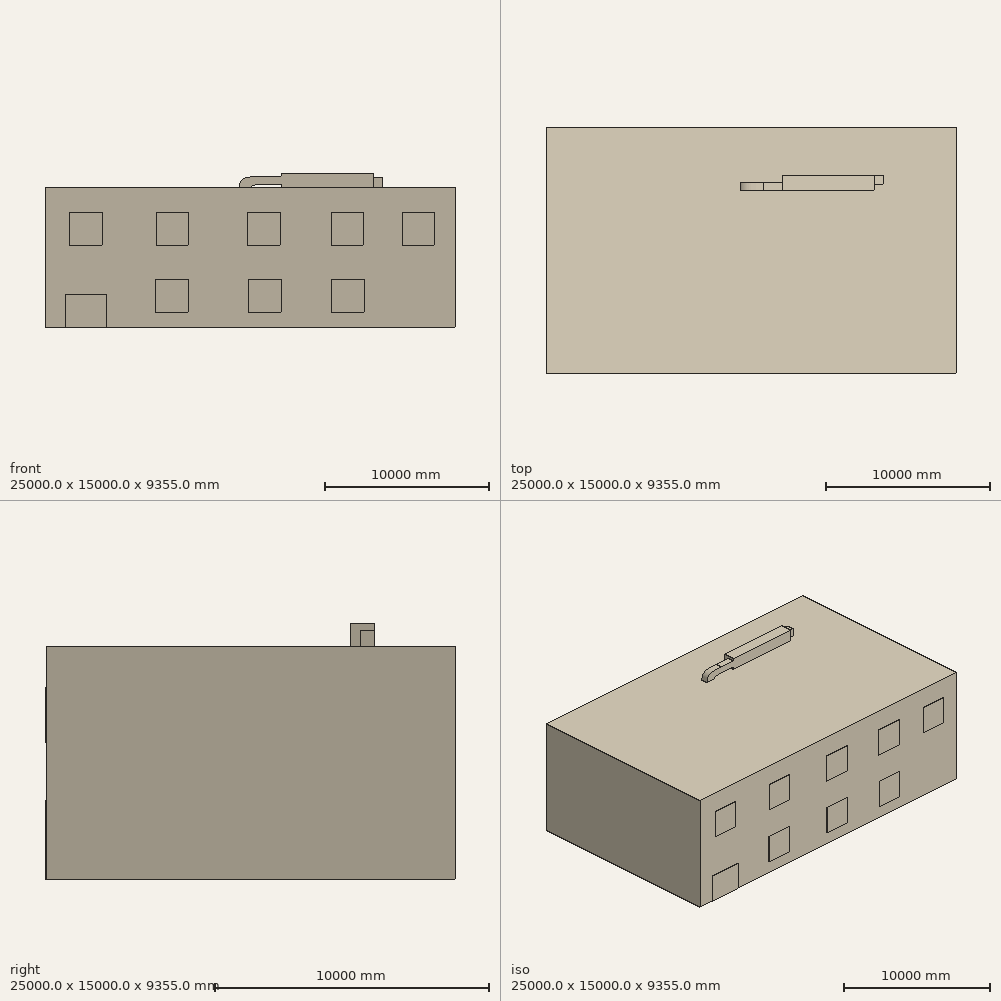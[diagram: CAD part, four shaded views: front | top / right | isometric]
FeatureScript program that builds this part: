
annotation { "Feature Type Name" : "Feature", "Feature Type Description" : "" }
export const myFeature = defineFeature(function(context is Context, id is Id, definition is map)
    precondition{}
    {
        {
            var Q0;
            Q0=qCreatedBy(makeId("Top.planeOp"),FACE);
            var sketch = newSketch(context, id + "F0", { "sketchPlane" : qUnion([Q0])});
            skLineSegment(sketch, "E0.bottom", {"start": v(0, 0) * mm, "end": v(25000, 0) * mm});
            skLineSegment(sketch, "E0.top", {"start": v(0, 15000) * mm, "end": v(25000, 15000) * mm});
            skLineSegment(sketch, "E0.left", {"start": v(0, 0) * mm, "end": v(0, 15000) * mm});
            skLineSegment(sketch, "E0.right", {"start": v(25000, 0) * mm, "end": v(25000, 15000) * mm});
            skSolve(sketch);
        }
        {
            var Q0;
            Q0 = qSketchRegion(id + "F0", true);
            extrude(context, id + "F1", {"entities" : qUnion([Q0]), "depth" : 500 * mm, "offsetDistance" : 25 * mm});
        }
        {
            var Q0;
            Q0=makeQuery(id+"F1.opExtrude","CAP_FACE",FACE,{"disambiguationData":[OSD([sQuery(id+"F0.wireOp",EDGE,"E0.bottom"),sQuery(id+"F0.wireOp",EDGE,"E0.top"),sQuery(id+"F0.wireOp",EDGE,"E0.left"),sQuery(id+"F0.wireOp",EDGE,"E0.right")])],"isStart":true});
            var sketch = newSketch(context, id + "F2", { "sketchPlane" : qUnion([Q0])});
            skLineSegment(sketch, "E1.bottom", {"start": v(0, -15000) * mm, "end": v(25000, -15000) * mm});
            skLineSegment(sketch, "E1.top", {"start": v(0, 0) * mm, "end": v(25000, 0) * mm});
            skLineSegment(sketch, "E1.left", {"start": v(0, -15000) * mm, "end": v(0, 0) * mm});
            skLineSegment(sketch, "E1.right", {"start": v(25000, -15000) * mm, "end": v(25000, 0) * mm});
            skLineSegment(sketch, "E2.bottom", {"start": v(400, -14600) * mm, "end": v(24600, -14600) * mm});
            skLineSegment(sketch, "E2.top", {"start": v(400, -400) * mm, "end": v(24600, -400) * mm});
            skLineSegment(sketch, "E2.left", {"start": v(400, -14600) * mm, "end": v(400, -400) * mm});
            skLineSegment(sketch, "E2.right", {"start": v(24600, -14600) * mm, "end": v(24600, -400) * mm});
            skSolve(sketch);
        }
        {
            var Q0;
            Q0 = qSketchRegion(id + "F2", true);
            extrude(context, id + "F3", {"entities" : qUnion([Q0]), "operationType" : NewBodyOperationType.ADD, "depth" : 8000 * mm, "offsetDistance" : 25 * mm});
        }
        {
            var Q0;
            Q0=makeQuery(id+"F3.boolean.opBoolean","MERGE",FACE,{"derivedFrom":[makeQuery(id+"F1.opExtrude","SWEPT_FACE",FACE,{"disambiguationData":[OSD([sQuery(id+"F0.wireOp",EDGE,"E0.bottom")])]}),makeQuery(id+"F3.opExtrude","SWEPT_FACE",FACE,{"disambiguationData":[OSD([sQuery(id+"F2.wireOp",EDGE,"E1.top")])]})]});
            var sketch = newSketch(context, id + "F4", { "sketchPlane" : qUnion([Q0])});
            skLineSegment(sketch, "E3.bottom", {"start": v(1471.7, -997.31) * mm, "end": v(3471.7, -997.31) * mm});
            skLineSegment(sketch, "E3.top", {"start": v(1471.7, -2997.31) * mm, "end": v(3471.7, -2997.31) * mm});
            skLineSegment(sketch, "E3.left", {"start": v(1471.7, -997.31) * mm, "end": v(1471.7, -2997.31) * mm});
            skLineSegment(sketch, "E3.right", {"start": v(3471.7, -997.31) * mm, "end": v(3471.7, -2997.31) * mm});
            skLineSegment(sketch, "E4", {"start": v(0, -2997.31) * mm, "end": v(25000, -2997.31) * mm, "construction": true});
            skLineSegment(sketch, "E5", {"start": v(25000, -4809.9) * mm, "end": v(25000, -7114.06) * mm, "construction": true});
            skLineSegment(sketch, "E6.bottom", {"start": v(6740.53, -997.31) * mm, "end": v(8740.53, -997.31) * mm});
            skLineSegment(sketch, "E6.top", {"start": v(6740.53, -2997.31) * mm, "end": v(8740.53, -2997.31) * mm});
            skLineSegment(sketch, "E6.left", {"start": v(6740.53, -997.31) * mm, "end": v(6740.53, -2997.31) * mm});
            skLineSegment(sketch, "E6.right", {"start": v(8740.53, -997.31) * mm, "end": v(8740.53, -2997.31) * mm});
            skLineSegment(sketch, "E7.bottom", {"start": v(12347.3, -997.31) * mm, "end": v(14347.3, -997.31) * mm});
            skLineSegment(sketch, "E7.top", {"start": v(12347.3, -2997.31) * mm, "end": v(14347.3, -2997.31) * mm});
            skLineSegment(sketch, "E7.left", {"start": v(12347.3, -997.31) * mm, "end": v(12347.3, -2997.31) * mm});
            skLineSegment(sketch, "E7.right", {"start": v(14347.3, -997.31) * mm, "end": v(14347.3, -2997.31) * mm});
            skLineSegment(sketch, "E8.bottom", {"start": v(17416.42, -997.31) * mm, "end": v(19416.42, -997.31) * mm});
            skLineSegment(sketch, "E8.top", {"start": v(17416.42, -2997.31) * mm, "end": v(19416.42, -2997.31) * mm});
            skLineSegment(sketch, "E8.left", {"start": v(17416.42, -997.31) * mm, "end": v(17416.42, -2997.31) * mm});
            skLineSegment(sketch, "E8.right", {"start": v(19416.42, -997.31) * mm, "end": v(19416.42, -2997.31) * mm});
            skLineSegment(sketch, "E9", {"start": v(5204.43, 500) * mm, "end": v(5204.43, -8000) * mm, "construction": true});
            skLineSegment(sketch, "E10", {"start": v(10288.92, 500) * mm, "end": v(10288.92, -8000) * mm, "construction": true});
            skLineSegment(sketch, "E11", {"start": v(16033.93, 500) * mm, "end": v(16033.93, -8000) * mm, "construction": true});
            skLineSegment(sketch, "E12", {"start": v(16033.93, -8000) * mm, "end": v(20888, -8000) * mm, "construction": true});
            skLineSegment(sketch, "E13", {"start": v(20888, -8000) * mm, "end": v(20888, 500) * mm, "construction": true});
            skLineSegment(sketch, "E14.bottom", {"start": v(21748.22, -997.31) * mm, "end": v(23748.22, -997.31) * mm});
            skLineSegment(sketch, "E14.top", {"start": v(21748.22, -2997.31) * mm, "end": v(23748.22, -2997.31) * mm});
            skLineSegment(sketch, "E14.left", {"start": v(21748.22, -997.31) * mm, "end": v(21748.22, -2997.31) * mm});
            skLineSegment(sketch, "E14.right", {"start": v(23748.22, -997.31) * mm, "end": v(23748.22, -2997.31) * mm});
            skLineSegment(sketch, "E15.bottom", {"start": v(1195.2, -6000) * mm, "end": v(3695.2, -6000) * mm});
            skLineSegment(sketch, "E15.top", {"start": v(1195.2, -8000) * mm, "end": v(3695.2, -8000) * mm});
            skLineSegment(sketch, "E15.left", {"start": v(1195.2, -6000) * mm, "end": v(1195.2, -8000) * mm});
            skLineSegment(sketch, "E15.right", {"start": v(3695.2, -6000) * mm, "end": v(3695.2, -8000) * mm});
            skLineSegment(sketch, "E16.bottom", {"start": v(6709.8, -5114.06) * mm, "end": v(8709.8, -5114.06) * mm});
            skLineSegment(sketch, "E16.top", {"start": v(6709.8, -7114.06) * mm, "end": v(8709.8, -7114.06) * mm});
            skLineSegment(sketch, "E16.left", {"start": v(6709.8, -5114.06) * mm, "end": v(6709.8, -7114.06) * mm});
            skLineSegment(sketch, "E16.right", {"start": v(8709.8, -5114.06) * mm, "end": v(8709.8, -7114.06) * mm});
            skLineSegment(sketch, "E17.bottom", {"start": v(12362.65, -5114.06) * mm, "end": v(14362.65, -5114.06) * mm});
            skLineSegment(sketch, "E17.top", {"start": v(12362.65, -7114.06) * mm, "end": v(14362.65, -7114.06) * mm});
            skLineSegment(sketch, "E17.left", {"start": v(12362.65, -5114.06) * mm, "end": v(12362.65, -7114.06) * mm});
            skLineSegment(sketch, "E17.right", {"start": v(14362.65, -5114.06) * mm, "end": v(14362.65, -7114.06) * mm});
            skLineSegment(sketch, "E18.bottom", {"start": v(17462.5, -5114.06) * mm, "end": v(19462.5, -5114.06) * mm});
            skLineSegment(sketch, "E18.top", {"start": v(17462.5, -7114.06) * mm, "end": v(19462.5, -7114.06) * mm});
            skLineSegment(sketch, "E18.left", {"start": v(17462.5, -5114.06) * mm, "end": v(17462.5, -7114.06) * mm});
            skLineSegment(sketch, "E18.right", {"start": v(19462.5, -5114.06) * mm, "end": v(19462.5, -7114.06) * mm});
            skSolve(sketch);
        }
        {
            var Q0;
            Q0=makeQuery(id+"F4.imprint","IMPRINT",FACE,{"disambiguationData":[TD([[makeQuery(id+"F4.imprint","IMPRINT",EDGE,{"derivedFrom":sQuery(id+"F4.wireOp",EDGE,"E3.bottom")}),1.0]])]});
            extrude(context, id + "F5", {"entities" : qUnion([Q0]), "operationType" : NewBodyOperationType.REMOVE, "oppositeDirection" : true, "depth" : 25 * mm, "offsetDistance" : 25 * mm});
        }
        {
            var Q0;
            Q0=makeQuery(id+"F1.opExtrude","CAP_FACE",FACE,{"disambiguationData":[OSD([sQuery(id+"F0.wireOp",EDGE,"E0.bottom"),sQuery(id+"F0.wireOp",EDGE,"E0.top"),sQuery(id+"F0.wireOp",EDGE,"E0.left"),sQuery(id+"F0.wireOp",EDGE,"E0.right")])],"isStart":false});
            var sketch = newSketch(context, id + "F6", { "sketchPlane" : qUnion([Q0])});
            skLineSegment(sketch, "E19.bottom", {"start": v(14416.46, 12043.64) * mm, "end": v(19974.46, 12043.64) * mm});
            skLineSegment(sketch, "E19.top", {"start": v(14416.46, 11163.64) * mm, "end": v(19974.46, 11163.64) * mm});
            skLineSegment(sketch, "E19.left", {"start": v(14416.46, 12043.64) * mm, "end": v(14416.46, 11163.64) * mm});
            skLineSegment(sketch, "E19.right", {"start": v(19974.46, 12043.64) * mm, "end": v(19974.46, 11163.64) * mm});
            skSolve(sketch);
        }
        {
            var Q0;
            Q0 = qSketchRegion(id + "F6", true);
            extrude(context, id + "F7", {"entities" : qUnion([Q0]), "operationType" : NewBodyOperationType.ADD, "depth" : 855 * mm, "offsetDistance" : 25 * mm});
        }
        {
            var Q0;
            Q0=makeQuery(id+"F1.opExtrude","CAP_FACE",FACE,{"disambiguationData":[OSD([sQuery(id+"F0.wireOp",EDGE,"E0.bottom"),sQuery(id+"F0.wireOp",EDGE,"E0.top"),sQuery(id+"F0.wireOp",EDGE,"E0.left"),sQuery(id+"F0.wireOp",EDGE,"E0.right")])],"isStart":false});
            var sketch = newSketch(context, id + "F8", { "sketchPlane" : qUnion([Q0])});
            skLineSegment(sketch, "E20.bottom", {"start": v(19974.46, 12043.64) * mm, "end": v(20574.46, 12043.64) * mm});
            skLineSegment(sketch, "E20.top", {"start": v(19974.46, 11510.8) * mm, "end": v(20574.46, 11510.8) * mm});
            skLineSegment(sketch, "E20.left", {"start": v(19974.46, 12043.64) * mm, "end": v(19974.46, 11510.8) * mm});
            skLineSegment(sketch, "E20.right", {"start": v(20574.46, 12043.64) * mm, "end": v(20574.46, 11510.8) * mm});
            skSolve(sketch);
        }
        {
            var Q0;
            Q0 = qSketchRegion(id + "F8", true);
            extrude(context, id + "F9", {"entities" : qUnion([Q0]), "operationType" : NewBodyOperationType.ADD, "depth" : 600 * mm, "offsetDistance" : 25 * mm});
        }
        {
            var Q0;
            Q0=makeQuery(id+"F7.opExtrude","SWEPT_FACE",FACE,{"disambiguationData":[OSD([sQuery(id+"F6.wireOp",EDGE,"E19.top")])]});
            var sketch = newSketch(context, id + "F10", { "sketchPlane" : qUnion([Q0])});
            skLineSegment(sketch, "E21.bottom", {"start": v(14416.46, 1182.3) * mm, "end": v(13218.94, 1182.3) * mm});
            skLineSegment(sketch, "E21.top", {"start": v(14416.46, 708.1) * mm, "end": v(13218.94, 708.1) * mm});
            skLineSegment(sketch, "E21.left", {"start": v(14416.46, 1182.3) * mm, "end": v(14416.46, 708.1) * mm});
            skLineSegment(sketch, "E21.right", {"start": v(13218.94, 1182.3) * mm, "end": v(13218.94, 708.1) * mm});
            skFitSpline(sketch, "E22", {"points": [v(13218.94, 1182.3) * mm, v(11818.96, 459.72) * mm], "startDerivative": vector(-2912.87, 135.48) * mm, "endDerivative": vector(67.74, -1829.01) * mm});
            skFitSpline(sketch, "E23", {"points": [v(13218.94, 708.1) * mm, v(12518.95, 482.3) * mm], "startDerivative": vector(-1016.12, -67.74) * mm, "endDerivative": vector(0, -609.67) * mm});
            skLineSegment(sketch, "E24", {"start": v(11818.96, 459.72) * mm, "end": v(12518.95, 482.3) * mm});
            skSolve(sketch);
        }
        {
            var Q0;
            Q0 = qSketchRegion(id + "F10", true);
            extrude(context, id + "F11", {"entities" : qUnion([Q0]), "operationType" : NewBodyOperationType.ADD, "oppositeDirection" : true, "depth" : 500 * mm, "offsetDistance" : 25 * mm});
        }
    });
